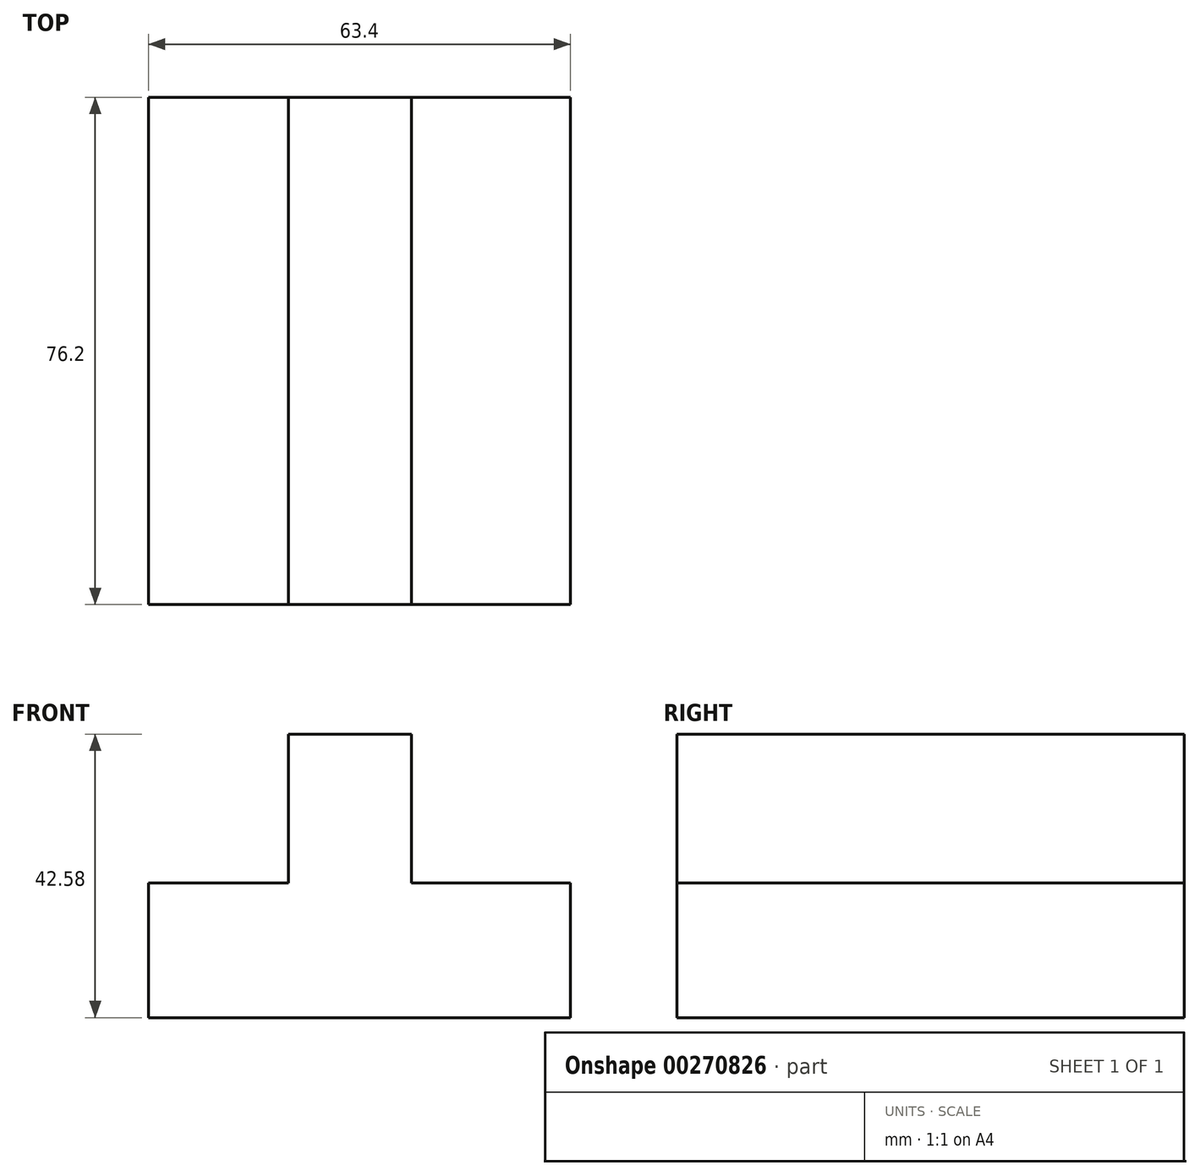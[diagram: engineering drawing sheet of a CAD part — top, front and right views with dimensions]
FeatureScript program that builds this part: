
annotation { "Feature Type Name" : "Feature", "Feature Type Description" : "" }
export const myFeature = defineFeature(function(context is Context, id is Id, definition is map)
    precondition{}
    {
        {
            var Q0;
            Q0=qCreatedBy(makeId("Front.planeOp"),FACE);
            var sketch = newSketch(context, id + "F0", { "sketchPlane" : qUnion([Q0])});
            skLineSegment(sketch, "E0", {"start": v(-75.8, 0) * mm, "end": v(-75.8, 20.24) * mm});
            skLineSegment(sketch, "E1", {"start": v(-75.8, 20.24) * mm, "end": v(-54.8, 20.24) * mm});
            skLineSegment(sketch, "E2", {"start": v(-54.8, 20.24) * mm, "end": v(-54.8, 42.58) * mm});
            skLineSegment(sketch, "E3", {"start": v(-54.8, 42.58) * mm, "end": v(-36.28, 42.58) * mm});
            skLineSegment(sketch, "E4", {"start": v(-36.28, 42.58) * mm, "end": v(-36.28, 20.24) * mm});
            skLineSegment(sketch, "E5", {"start": v(-36.28, 20.24) * mm, "end": v(-12.41, 20.24) * mm});
            skLineSegment(sketch, "E6", {"start": v(-12.41, 20.24) * mm, "end": v(-12.41, 0) * mm});
            skLineSegment(sketch, "E7", {"start": v(-12.41, 0) * mm, "end": v(-75.8, 0) * mm});
            skSolve(sketch);
        }
        {
            var Q0;
            Q0 = qSketchRegion(id + "F0", true);
            extrude(context, id + "F1", {"entities" : qUnion([Q0]), "depth" : 76.2 * mm});
        }
    });
